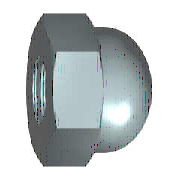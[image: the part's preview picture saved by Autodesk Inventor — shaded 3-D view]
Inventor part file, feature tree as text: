
AUTODESK INVENTOR PART (.ipt)
format: ipt  version: 2021.2 (Build 252289000, 289)  size: 210,432 bytes
history: native  units: mm (DEFAULTED — no unit token found)
features: sketch x4, other x3, extrude x1, hole x1, plane x1
ambient origin geometry x7: Origin, YZ Plane, XZ Plane, X Axis, Y Axis, Z Axis, Center Point
bodies: Solid1 (feature_tree)
feature tree (10):
  extrude  "Базовый элемент"  Depth=8.082904mm
  other  "Наконечник"
  hole  "Резьба"  [1 undecoded]
  other  "Фаска1"
  other  "Work Axis1"
  plane  "Work Plane1"
  sketch  "Эскиз1"
  sketch  "Эскиз4"
  sketch  "Эскиз2"
  sketch  "Эскиз3"
note: 1 required parameter value undecoded (feature->parameter linkage not recoverable at this tier; creation-order binding heuristic only, values carry confidence <= 0.55)
